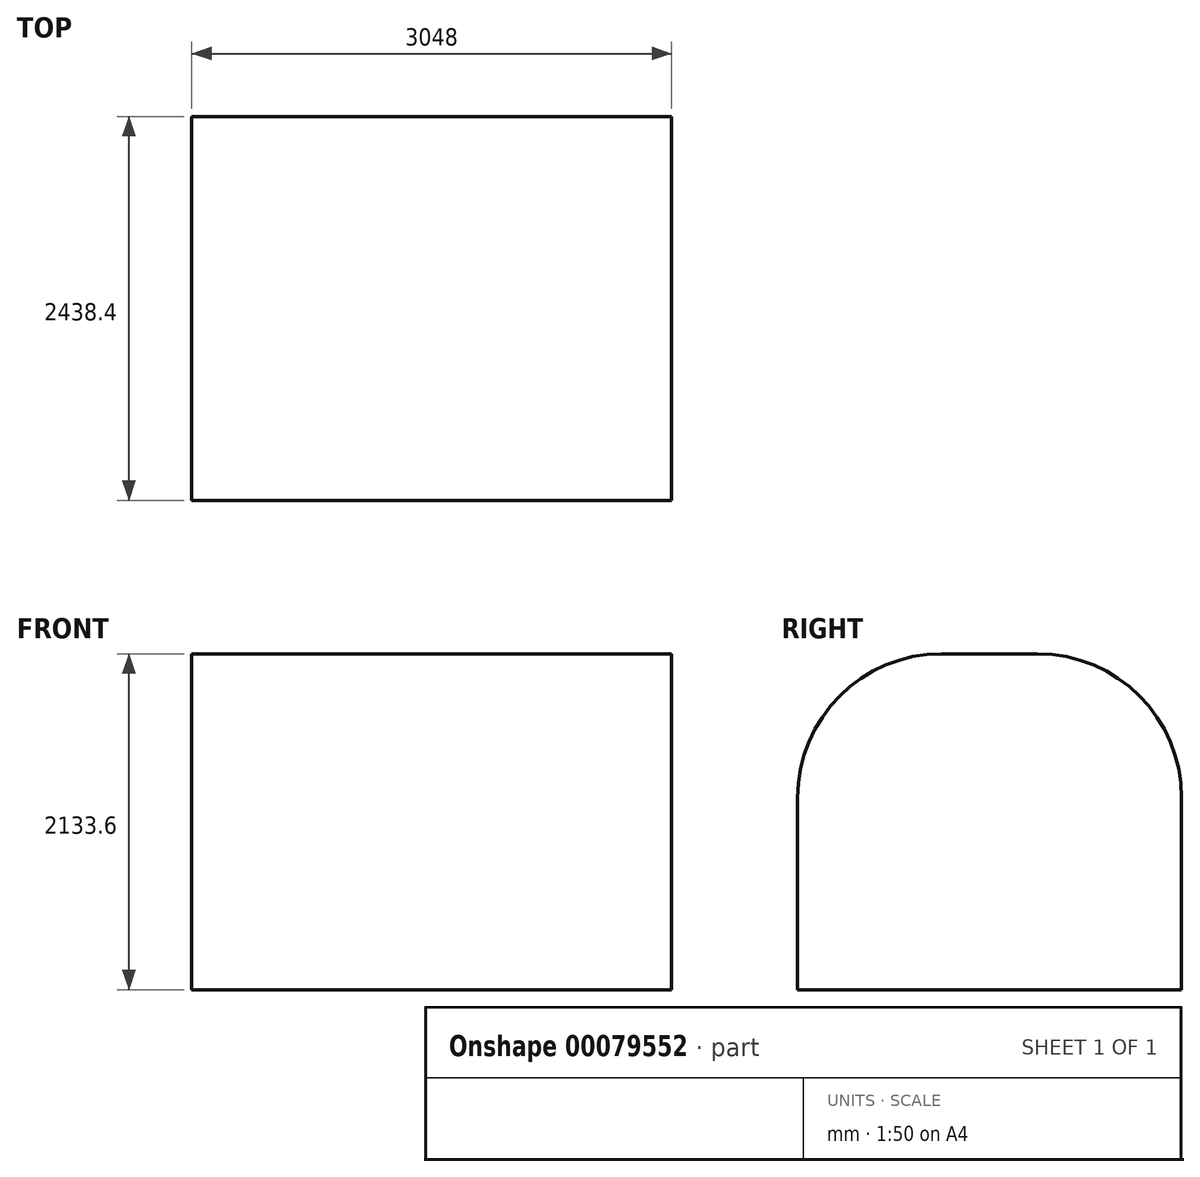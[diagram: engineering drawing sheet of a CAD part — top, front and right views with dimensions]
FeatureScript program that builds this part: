
annotation { "Feature Type Name" : "Feature", "Feature Type Description" : "" }
export const myFeature = defineFeature(function(context is Context, id is Id, definition is map)
    precondition{}
    {
        {
            var Q0;
            Q0=qCreatedBy(makeId("Top.planeOp"),FACE);
            var sketch = newSketch(context, id + "F0", { "sketchPlane" : qUnion([Q0])});
            skLineSegment(sketch, "E0.bottom", {"start": v(1524, 1219.2) * mm, "end": v(-1524, 1219.2) * mm});
            skLineSegment(sketch, "E0.top", {"start": v(1524, -1219.2) * mm, "end": v(-1524, -1219.2) * mm});
            skLineSegment(sketch, "E0.left", {"start": v(1524, 1219.2) * mm, "end": v(1524, -1219.2) * mm});
            skLineSegment(sketch, "E0.right", {"start": v(-1524, 1219.2) * mm, "end": v(-1524, -1219.2) * mm});
            skPoint(sketch, "E0.middle", {"position": v(0, 0) * mm});
            skSolve(sketch);
        }
        {
            var Q0;
            Q0 = qSketchRegion(id + "F0", true);
            extrude(context, id + "F1", {"entities" : qUnion([Q0]), "depth" : 2133.6 * mm});
        }
        {
            var Q0;
            Q0=makeQuery(id+"F1.opExtrude","CAP_EDGE",EDGE,{"disambiguationData":[OSD([sQuery(id+"F0.wireOp",EDGE,"E0.bottom")])],"isStart":false});
            fillet(context, id + "F2", {"entities" : qUnion([Q0]), "radius" : 914.4 * mm, "tangentPropagation" : true, "allowEdgeOverflow" : false});
        }
        {
            var Q0;
            Q0=makeQuery(id+"F1.opExtrude","CAP_EDGE",EDGE,{"disambiguationData":[OSD([sQuery(id+"F0.wireOp",EDGE,"E0.top")])],"isStart":false});
            fillet(context, id + "F3", {"entities" : qUnion([Q0]), "radius" : 914.4 * mm, "tangentPropagation" : true, "allowEdgeOverflow" : false});
        }
    });
